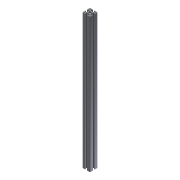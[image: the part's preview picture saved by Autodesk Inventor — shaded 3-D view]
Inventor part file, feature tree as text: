
AUTODESK INVENTOR PART (.ipt)
format: ipt  version: 2016 (Build 200138000, 138)  size: 182,272 bytes
history: native  units: mm
features: other x42, sketch x5, hole x4, extrude x1
ambient origin geometry x8: Origin, YZ Plane, XZ Plane, XY Plane, X Axis, Y Axis, Z Axis, Center Point
bodies: Solid1 (feature_tree)
feature tree (52):
  extrude  "Extrusion1"  [1 undecoded]
  hole  "Drilling 1"  [1 undecoded]
  hole  "Drilling 2"  [1 undecoded]
  hole  "Drilling 3"  [1 undecoded]
  hole  "Drilling 4"  [1 undecoded]
  other  "side_4d_XY"
  other  "side_4d_YZ"
  other  "side_4d_ZX"
  other  "side_4d_X"
  other  "side_4d_Y"
  other  "side_4d_Z"
  other  "side_4d_Center"
  other  "side_1a_XY"
  other  "side_1a_YZ"
  other  "side_1a_ZX"
  other  "side_1a_X"
  other  "side_1a_Y"
  other  "side_1a_Z"
  other  "side_1a_Center"
  other  "side_2b_XY"
  other  "side_2b_YZ"
  other  "side_2b_ZX"
  other  "side_2b_X"
  other  "side_2b_Y"
  other  "side_2b_Z"
  other  "side_2b_Center"
  other  "side_3c_XY"
  other  "side_3c_YZ"
  other  "side_3c_ZX"
  other  "side_3c_X"
  other  "side_3c_Y"
  other  "side_3c_Z"
  other  "side_3c_Center"
  other  "end_XY"
  other  "end_YZ"
  other  "end_ZX"
  other  "end_X"
  other  "end_Y"
  other  "end_Z"
  other  "end_Center"
  other  "start_XY"
  other  "start_YZ"
  other  "start_ZX"
  other  "start_X"
  other  "start_Y"
  other  "start_Z"
  other  "start_Center"
  sketch  "Skizze_1"  dims[d0=700.0mm d1=0.0mm]
  sketch  "Sketch2"  dims[d2=5.0mm d3=6.0mm d4=4.0mm d5=2.0mm d6=90.0deg d7=6000.0mm d8=0.0mm]
  sketch  "Sketch3"  dims[d9=5.0mm d10=6.0mm d11=4.0mm d12=2.0mm d13=90.0deg d14=6000.0mm d15=0.0mm]
  sketch  "Sketch4"  dims[d16=5.0mm d17=6.0mm d18=4.0mm d19=2.0mm d20=90.0deg d21=6000.0mm d22=0.0mm]
  sketch  "Sketch5"  dims[d23=5.0mm d24=6.0mm d25=4.0mm d26=2.0mm d27=90.0deg d28=6000.0mm d29=0.0mm]
note: 5 required parameter values undecoded (feature->parameter linkage not recoverable at this tier; creation-order binding heuristic only, values carry confidence <= 0.55)
